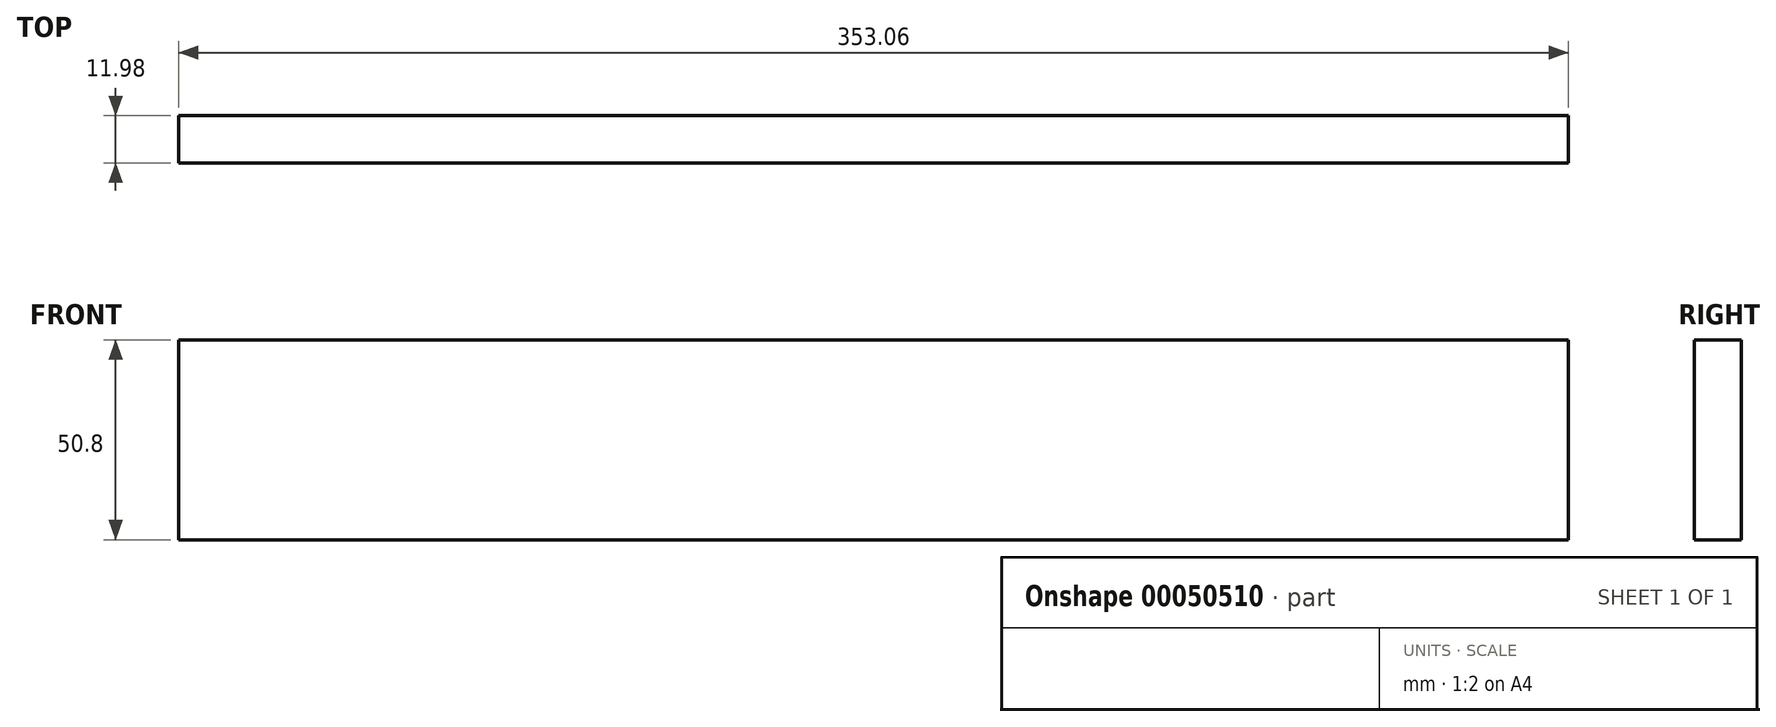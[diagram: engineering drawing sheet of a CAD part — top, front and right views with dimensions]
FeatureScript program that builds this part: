
annotation { "Feature Type Name" : "Feature", "Feature Type Description" : "" }
export const myFeature = defineFeature(function(context is Context, id is Id, definition is map)
    precondition{}
    {
        {
            var Q0;
            Q0=qCreatedBy(makeId("Front.planeOp"),FACE);
            var sketch = newSketch(context, id + "F0", { "sketchPlane" : qUnion([Q0])});
            skLineSegment(sketch, "E0.rect.bottom", {"start": v(176.53, 25.4) * mm, "end": v(-176.53, 25.4) * mm});
            skLineSegment(sketch, "E0.rect.top", {"start": v(176.53, -25.4) * mm, "end": v(-176.53, -25.4) * mm});
            skLineSegment(sketch, "E0.rect.left", {"start": v(176.53, 25.4) * mm, "end": v(176.53, -25.4) * mm});
            skLineSegment(sketch, "E0.rect.right", {"start": v(-176.53, 25.4) * mm, "end": v(-176.53, -25.4) * mm});
            skPoint(sketch, "E0.rect.middle", {"position": v(0, 0) * mm});
            skSolve(sketch);
        }
        {
            var Q0;
            Q0=qSketchRegion(id+"F0",true);
            extrude(context, id + "F1", {"entities" : qUnion([Q0]), "endBound" : BoundingType.SYMMETRIC, "depth" : 12 * mm});
        }
    });
